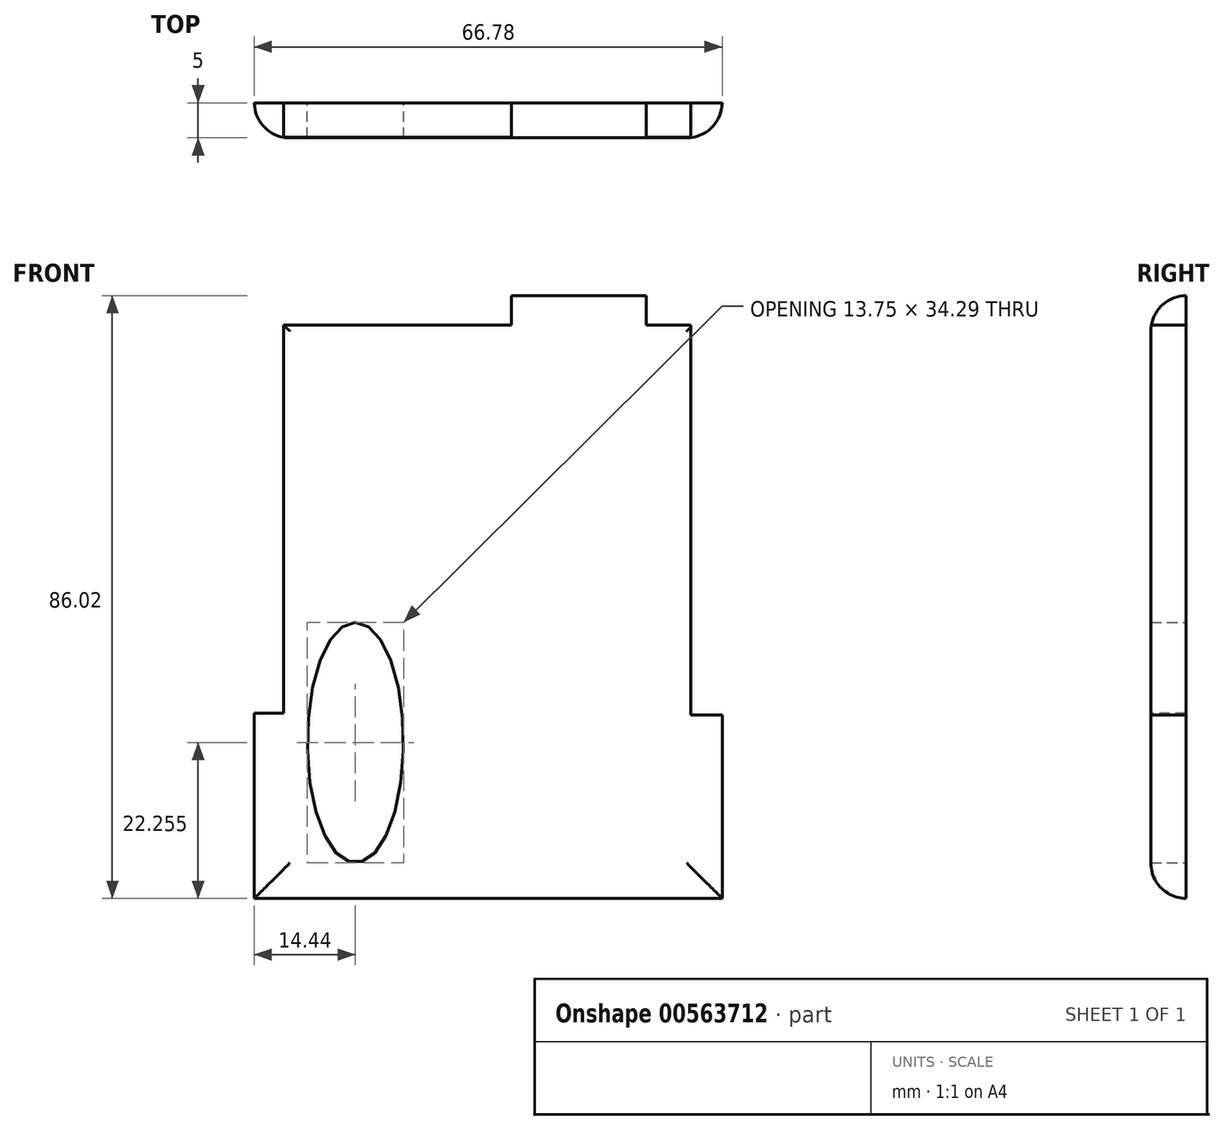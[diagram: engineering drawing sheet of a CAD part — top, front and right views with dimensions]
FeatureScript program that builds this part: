
annotation { "Feature Type Name" : "Feature", "Feature Type Description" : "" }
export const myFeature = defineFeature(function(context is Context, id is Id, definition is map)
    precondition{}
    {
        {
            var Q0;
            Q0=qCreatedBy(makeId("Front.planeOp"),FACE);
            var sketch = newSketch(context, id + "F0", { "sketchPlane" : qUnion([Q0])});
            skLineSegment(sketch, "E0.bottom", {"start": v(-33.39, 43.01) * mm, "end": v(33.39, 43.01) * mm});
            skLineSegment(sketch, "E0.top", {"start": v(-33.39, -43.01) * mm, "end": v(33.39, -43.01) * mm});
            skLineSegment(sketch, "E0.left", {"start": v(-33.39, 43.01) * mm, "end": v(-33.39, -43.01) * mm});
            skLineSegment(sketch, "E0.right", {"start": v(33.39, 43.01) * mm, "end": v(33.39, -43.01) * mm});
            skPoint(sketch, "E0.middle", {"position": v(0, 0) * mm});
            skSolve(sketch);
        }
        {
            var Q0;
            Q0=makeQuery(id+"F0.imprint","IMPRINT",FACE,{"disambiguationData":[TD([[makeQuery(id+"F0.imprint","IMPRINT",EDGE,{"derivedFrom":sQuery(id+"F0.wireOp",EDGE,"E0.bottom")}),-1.0]])]});
            extrude(context, id + "F1", {"entities" : qUnion([Q0]), "depth" : 5 * mm, "offsetDistance" : 25.4 * mm});
        }
        {
            var Q0;
            Q0=makeQuery(id+"F1.opExtrude","CAP_FACE",FACE,{"disambiguationData":[OSD([sQuery(id+"F0.wireOp",EDGE,"E0.bottom"),sQuery(id+"F0.wireOp",EDGE,"E0.top"),sQuery(id+"F0.wireOp",EDGE,"E0.left"),sQuery(id+"F0.wireOp",EDGE,"E0.right")])],"isStart":true});
            var sketch = newSketch(context, id + "F2", { "sketchPlane" : qUnion([Q0])});
            skEllipse(sketch, "E1", {"center": v(18.95, -20.75) * mm, "majorRadius": 17.14 * mm, "minorRadius": 6.87 * mm, "majorAxis": v(0, 1)});
            skSolve(sketch);
        }
        {
            var Q0;
            Q0=makeQuery(id+"F1.opExtrude","CAP_FACE",FACE,{"disambiguationData":[OSD([sQuery(id+"F0.wireOp",EDGE,"E0.bottom"),sQuery(id+"F0.wireOp",EDGE,"E0.top"),sQuery(id+"F0.wireOp",EDGE,"E0.left"),sQuery(id+"F0.wireOp",EDGE,"E0.right")])],"isStart":false});
            var sketch = newSketch(context, id + "F3", { "sketchPlane" : qUnion([Q0])});
            skLineSegment(sketch, "E2.bottom", {"start": v(33.39, -16.84) * mm, "end": v(28.88, -16.84) * mm});
            skLineSegment(sketch, "E2.top", {"start": v(33.39, 43.01) * mm, "end": v(28.88, 43.01) * mm});
            skLineSegment(sketch, "E2.left", {"start": v(33.39, -16.84) * mm, "end": v(33.39, 43.01) * mm});
            skLineSegment(sketch, "E2.right", {"start": v(28.88, -16.84) * mm, "end": v(28.88, 43.01) * mm});
            skLineSegment(sketch, "E3.bottom", {"start": v(33.39, 38.8) * mm, "end": v(22.56, 38.8) * mm});
            skLineSegment(sketch, "E3.top", {"start": v(33.39, 43.01) * mm, "end": v(22.56, 43.01) * mm});
            skLineSegment(sketch, "E3.left", {"start": v(33.39, 38.8) * mm, "end": v(33.39, 43.01) * mm});
            skLineSegment(sketch, "E3.right", {"start": v(22.56, 38.8) * mm, "end": v(22.56, 43.01) * mm});
            skLineSegment(sketch, "E4.bottom", {"start": v(3.3, 43.01) * mm, "end": v(-33.39, 43.01) * mm});
            skLineSegment(sketch, "E4.top", {"start": v(3.3, 38.8) * mm, "end": v(-33.39, 38.8) * mm});
            skLineSegment(sketch, "E4.left", {"start": v(3.3, 43.01) * mm, "end": v(3.3, 38.8) * mm});
            skLineSegment(sketch, "E4.right", {"start": v(-33.39, 43.01) * mm, "end": v(-33.39, 38.8) * mm});
            skLineSegment(sketch, "E5.bottom", {"start": v(-29.18, 43.01) * mm, "end": v(-33.39, 43.01) * mm});
            skLineSegment(sketch, "E5.top", {"start": v(-29.18, -16.54) * mm, "end": v(-33.39, -16.54) * mm});
            skLineSegment(sketch, "E5.left", {"start": v(-29.18, 43.01) * mm, "end": v(-29.18, -16.54) * mm});
            skLineSegment(sketch, "E5.right", {"start": v(-33.39, 43.01) * mm, "end": v(-33.39, -16.54) * mm});
            skSolve(sketch);
        }
        {
            var Q0;
            Q0 = qSketchRegion(id + "F3", true);
            extrude(context, id + "F4", {"entities" : qUnion([Q0]), "operationType" : NewBodyOperationType.REMOVE, "oppositeDirection" : true, "depth" : 25.4 * mm, "offsetDistance" : 25.4 * mm});
        }
        {
            var Q0;
            Q0 = qSketchRegion(id + "F2", true);
            extrude(context, id + "F5", {"entities" : qUnion([Q0]), "operationType" : NewBodyOperationType.REMOVE, "oppositeDirection" : true, "depth" : 25.4 * mm, "offsetDistance" : 25.4 * mm});
        }
        {
            var Q0;
            Q0=makeQuery(id+"F1.opExtrude","CAP_EDGE",EDGE,{"disambiguationData":[OSD([sQuery(id+"F0.wireOp",EDGE,"E0.top")])],"isStart":false});
            var Q1;
            Q1=makeQuery(id+"F1.opExtrude","CAP_EDGE",EDGE,{"disambiguationData":[OSD([sQuery(id+"F0.wireOp",EDGE,"E0.left")])],"isStart":false});
            var Q2;
            Q2=makeQuery(id+"F1.opExtrude","CAP_EDGE",EDGE,{"disambiguationData":[OSD([sQuery(id+"F0.wireOp",EDGE,"E0.right")])],"isStart":false});
            var Q3;
            Q3=makeQuery(id+"F1.opExtrude","CAP_EDGE",EDGE,{"disambiguationData":[OSD([sQuery(id+"F0.wireOp",EDGE,"E0.bottom")])],"isStart":false});
            fillet(context, id + "F6", {"entities" : qUnion([Q0, Q1, Q2, Q3]), "radius" : 5.08 * mm, "tangentPropagation" : true, "allowEdgeOverflow" : false});
        }
    });
